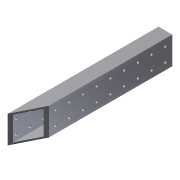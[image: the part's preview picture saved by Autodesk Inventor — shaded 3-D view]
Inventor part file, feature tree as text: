
AUTODESK INVENTOR PART (.ipt)
format: ipt  version: 2012 (Build 160160000, 160)  size: 137,216 bytes
history: native  units: in
note: dims shown in document units (in); Inventor stores cm internally (conversion verified against a paired STEP export)
features: extrude x3, sketch x3, shell x1, pattern_linear x1
ambient origin geometry x8: Origin, YZ Plane, XZ Plane, XY Plane, X Axis, Y Axis, Z Axis, Center Point
bodies: Solid1 (feature_tree)
feature tree (8):
  extrude  "Extrusion1"  Depth=2.0in
  shell  "Shell1"  Thickness=11.0in
  extrude  "Extrusion2"  Depth=0.1875in
  pattern_linear  "Rectangular Pattern1"  Spacing1=0.5in  [1 undecoded]
  extrude  "Extrusion3"  Depth=12.0in TaperAngle=0.0deg
  sketch  "Sketch1"  dims[d0=1.0in d1=2.0in d2=11.0in d3=0.0in]
  sketch  "Sketch2"  dims[d4=0.125in d5=0.1875in]
  sketch  "Sketch3"  dims[d6=0.5in d7=0.5in d8=12.0in d9=0.0in d10=4.3307in d12=1.0in d13=0.7874in d15=1.0in d16=2.0in d17=12.0in d18=0.0in]
note: 1 required parameter value undecoded (feature->parameter linkage not recoverable at this tier; creation-order binding heuristic only, values carry confidence <= 0.55)
